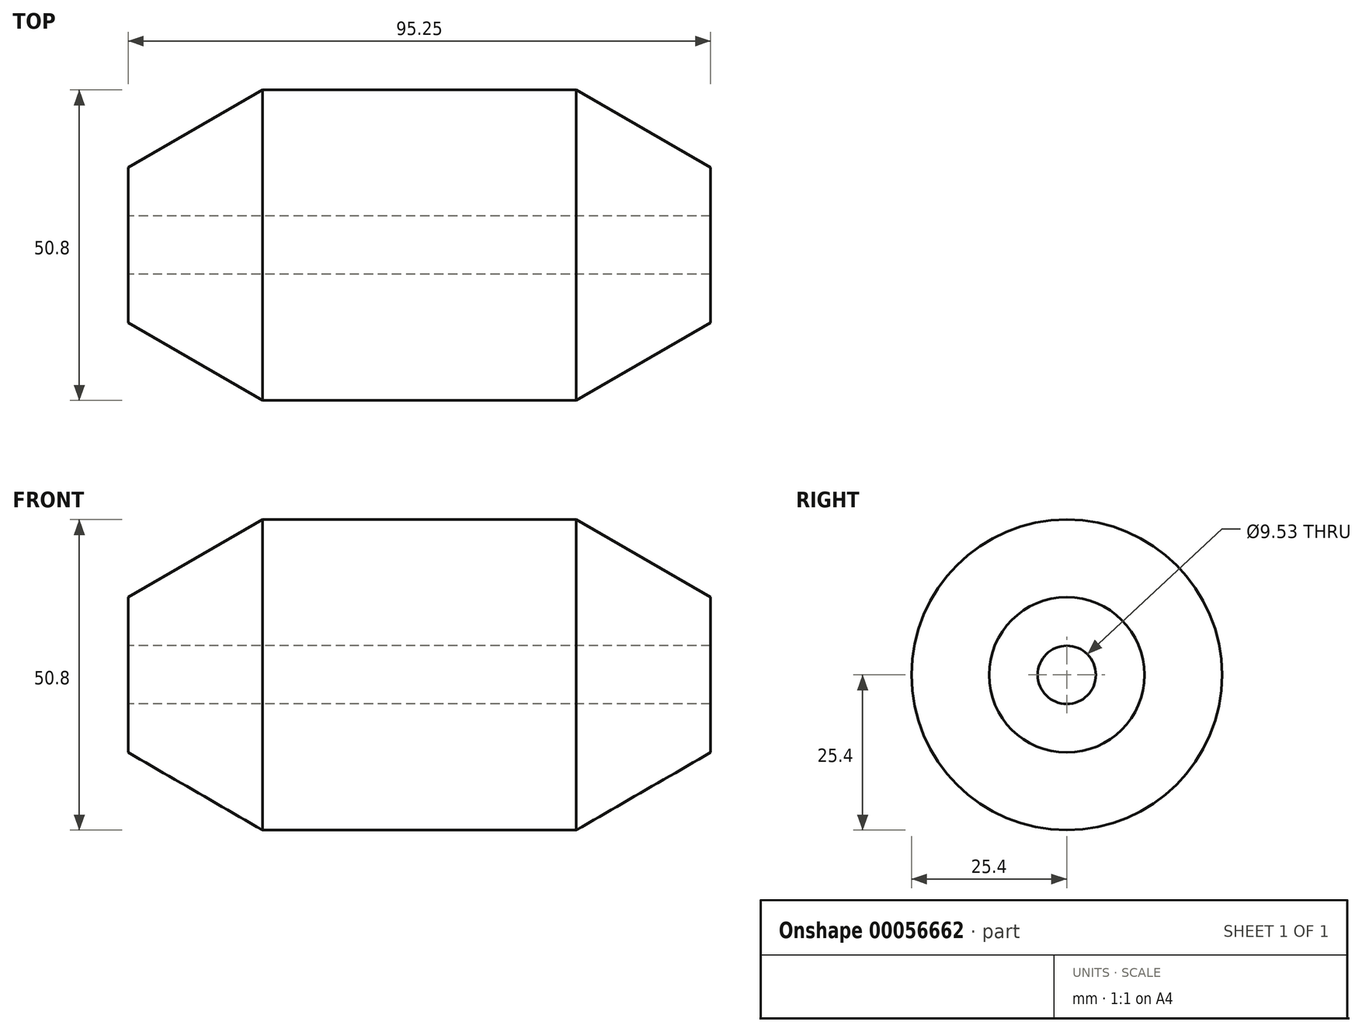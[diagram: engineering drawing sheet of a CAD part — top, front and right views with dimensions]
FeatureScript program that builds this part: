
annotation { "Feature Type Name" : "Feature", "Feature Type Description" : "" }
export const myFeature = defineFeature(function(context is Context, id is Id, definition is map)
    precondition{}
    {
        {
            var Q0;
            Q0=qCreatedBy(makeId("Front.planeOp"),FACE);
            var sketch = newSketch(context, id + "F0", { "sketchPlane" : qUnion([Q0])});
            skLineSegment(sketch, "E0", {"start": v(0, 0) * mm, "end": v(0, 12.7) * mm});
            skLineSegment(sketch, "E1", {"start": v(0, 12.7) * mm, "end": v(22, 25.4) * mm});
            skLineSegment(sketch, "E2", {"start": v(22, 25.4) * mm, "end": v(73.25, 25.4) * mm});
            skLineSegment(sketch, "E3", {"start": v(73.25, 25.4) * mm, "end": v(95.25, 12.7) * mm});
            skLineSegment(sketch, "E4", {"start": v(95.25, 12.7) * mm, "end": v(95.25, 0) * mm});
            skLineSegment(sketch, "E5", {"start": v(95.25, 0) * mm, "end": v(0, 0) * mm});
            skSolve(sketch);
        }
        {
            var Q0;
            Q0=makeQuery(id+"F0.imprint","IMPRINT",FACE,{"disambiguationData":[TD([[makeQuery(id+"F0.imprint","IMPRINT",EDGE,{"derivedFrom":sQuery(id+"F0.wireOp",EDGE,"E0")}),-1.0]])]});
            var Q1;
            Q1=sQuery(id+"F0.wireOp",EDGE,"E5");
            revolve(context, id + "F1", {"entities" : qUnion([Q0]), "axis" : qUnion([Q1]), "revolveType" : RevolveType.FULL});
        }
        {
            var Q0;
            Q0=makeQuery(id+"F1.opRevolve","SWEPT_FACE",FACE,{"disambiguationData":[OSD([sQuery(id+"F0.wireOp",EDGE,"E0")])]});
            var sketch = newSketch(context, id + "F2", { "sketchPlane" : qUnion([Q0])});
            skCircle(sketch, "E6", {"center": v(0, 0) * mm, "radius": 4.76 * mm});
            skSolve(sketch);
        }
        {
            var Q0;
            Q0 = qSketchRegion(id + "F2", true);
            extrude(context, id + "F3", {"entities" : qUnion([Q0]), "operationType" : NewBodyOperationType.REMOVE, "endBound" : BoundingType.THROUGH_ALL, "oppositeDirection" : true, "depth" : 25.4 * mm});
        }
    });
